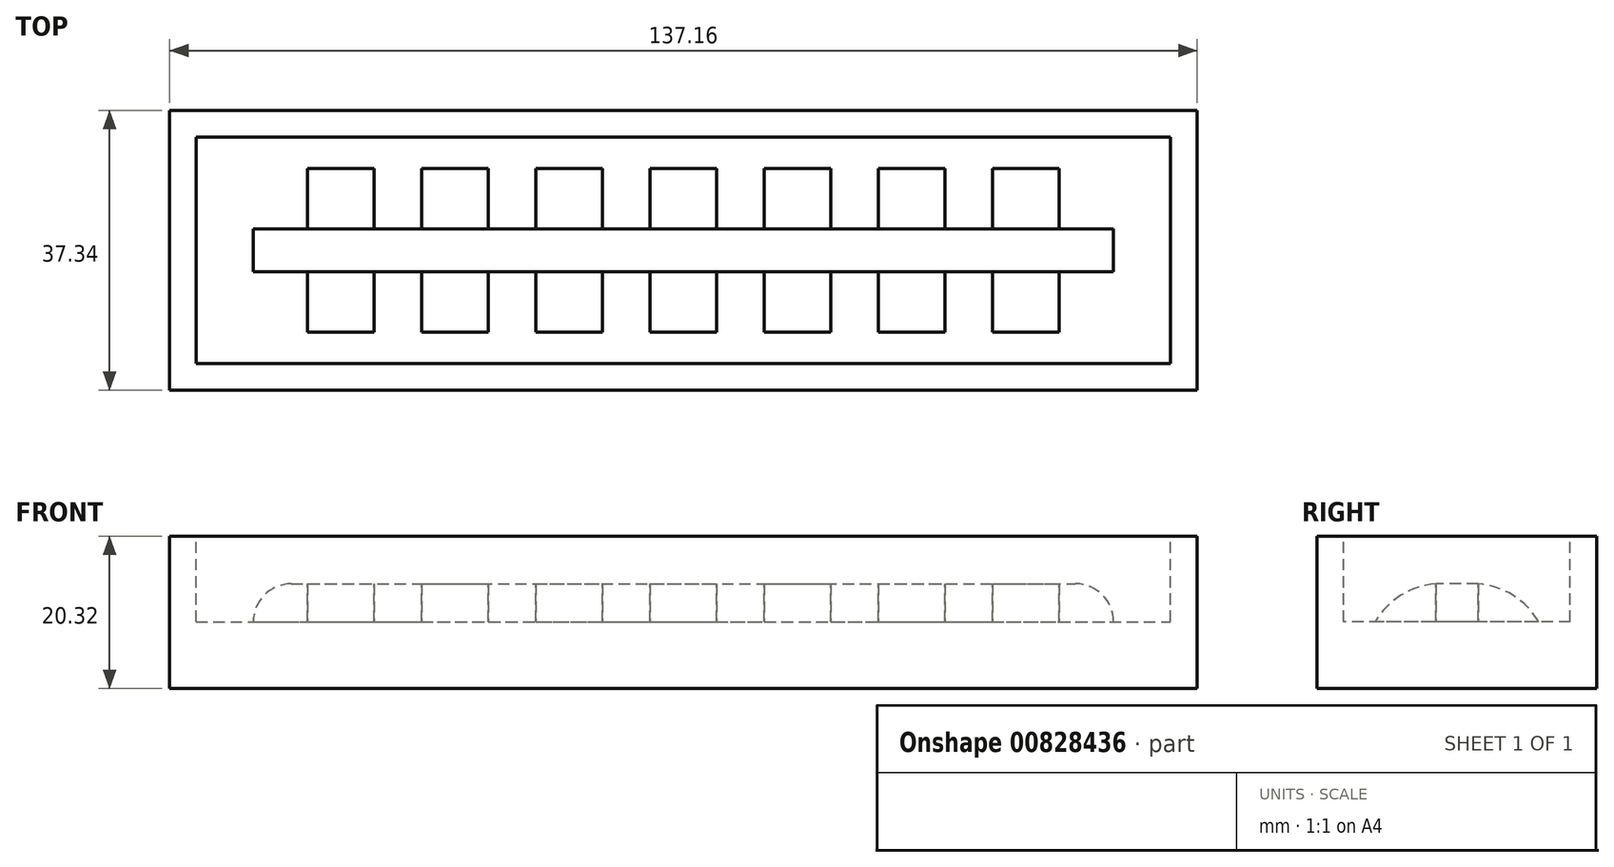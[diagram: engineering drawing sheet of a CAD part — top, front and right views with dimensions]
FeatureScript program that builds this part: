
annotation { "Feature Type Name" : "Feature", "Feature Type Description" : "" }
export const myFeature = defineFeature(function(context is Context, id is Id, definition is map)
    precondition{}
    {
        {
            var Q0;
            Q0=qCreatedBy(makeId("Top.planeOp"),FACE);
            var sketch = newSketch(context, id + "F0", { "sketchPlane" : qUnion([Q0])});
            skLineSegment(sketch, "E0.bottom", {"start": v(-68.58, 18.67) * mm, "end": v(68.58, 18.67) * mm});
            skLineSegment(sketch, "E0.top", {"start": v(-68.58, -18.67) * mm, "end": v(68.58, -18.67) * mm});
            skLineSegment(sketch, "E0.left", {"start": v(-68.58, 18.67) * mm, "end": v(-68.58, -18.67) * mm});
            skLineSegment(sketch, "E0.right", {"start": v(68.58, 18.67) * mm, "end": v(68.58, -18.67) * mm});
            skPoint(sketch, "E0.middle", {"position": v(0, 0) * mm});
            skSolve(sketch);
        }
        {
            var Q0;
            Q0=makeQuery(id+"F0.imprint","IMPRINT",FACE,{"disambiguationData":[TD([[makeQuery(id+"F0.imprint","IMPRINT",EDGE,{"derivedFrom":sQuery(id+"F0.wireOp",EDGE,"E0.bottom")}),-1.0]])]});
            extrude(context, id + "F1", {"entities" : qUnion([Q0]), "depth" : 20.32 * mm, "offsetDistance" : 25.4 * mm});
        }
        {
            var Q0;
            Q0=makeQuery(id+"F1.opExtrude","CAP_FACE",FACE,{"disambiguationData":[OSD([sQuery(id+"F0.wireOp",EDGE,"E0.bottom"),sQuery(id+"F0.wireOp",EDGE,"E0.top"),sQuery(id+"F0.wireOp",EDGE,"E0.left"),sQuery(id+"F0.wireOp",EDGE,"E0.right")])],"isStart":false});
            var sketch = newSketch(context, id + "F2", { "sketchPlane" : qUnion([Q0])});
            skLineSegment(sketch, "E1.bottom", {"start": v(-65.02, 15.11) * mm, "end": v(65.02, 15.11) * mm});
            skLineSegment(sketch, "E1.top", {"start": v(-65.02, -15.11) * mm, "end": v(65.02, -15.11) * mm});
            skLineSegment(sketch, "E1.left", {"start": v(-65.02, 15.11) * mm, "end": v(-65.02, -15.11) * mm});
            skLineSegment(sketch, "E1.right", {"start": v(65.02, 15.11) * mm, "end": v(65.02, -15.11) * mm});
            skPoint(sketch, "E1.middle", {"position": v(0, 0) * mm});
            skSolve(sketch);
        }
        {
            var Q0;
            Q0 = qSketchRegion(id + "F2", true);
            extrude(context, id + "F3", {"entities" : qUnion([Q0]), "operationType" : NewBodyOperationType.REMOVE, "oppositeDirection" : true, "depth" : 11.43 * mm, "offsetDistance" : 25.4 * mm});
        }
        {
            var Q0;
            Q0=makeQuery(id+"F3.boolean.opBoolean","COPY",FACE,{"derivedFrom":makeQuery(id+"F3.opExtrude","CAP_FACE",FACE,{"disambiguationData":[OSD([sQuery(id+"F2.wireOp",EDGE,"E1.bottom"),sQuery(id+"F2.wireOp",EDGE,"E1.top"),sQuery(id+"F2.wireOp",EDGE,"E1.left"),sQuery(id+"F2.wireOp",EDGE,"E1.right")])],"isStart":false})});
            var sketch = newSketch(context, id + "F4", { "sketchPlane" : qUnion([Q0])});
            skLineSegment(sketch, "E2.bottom", {"start": v(-4.44, 10.92) * mm, "end": v(4.45, 10.92) * mm});
            skLineSegment(sketch, "E2.top", {"start": v(-4.44, -10.92) * mm, "end": v(4.45, -10.92) * mm});
            skLineSegment(sketch, "E2.left", {"start": v(-4.44, 10.92) * mm, "end": v(-4.44, -10.92) * mm});
            skLineSegment(sketch, "E2.right", {"start": v(4.45, 10.92) * mm, "end": v(4.45, -10.92) * mm});
            skPoint(sketch, "E2.middle", {"position": v(0, 0) * mm});
            skPoint(sketch, "E3.endSnap0", {"position": v(0, -10.92) * mm});
            skPoint(sketch, "E4", {"position": v(-54.86, 0) * mm});
            skPoint(sketch, "E5", {"position": v(-45.72, 0) * mm});
            skPoint(sketch, "E6", {"position": v(-30.48, 0) * mm});
            skPoint(sketch, "E7", {"position": v(-15.24, 0) * mm});
            skPoint(sketch, "E8", {"position": v(15.24, 0) * mm});
            skPoint(sketch, "E8.positionSnap0", {"position": v(-4.44, 0) * mm});
            skPoint(sketch, "E9", {"position": v(30.48, 0) * mm});
            skPoint(sketch, "E10", {"position": v(45.72, 0) * mm});
            skPoint(sketch, "E11", {"position": v(54.86, 0) * mm});
            skLineSegment(sketch, "E12.bottom", {"start": v(10.8, 10.92) * mm, "end": v(19.69, 10.92) * mm});
            skLineSegment(sketch, "E12.top", {"start": v(10.8, -10.92) * mm, "end": v(19.69, -10.92) * mm});
            skLineSegment(sketch, "E12.left", {"start": v(10.8, 10.92) * mm, "end": v(10.8, -10.92) * mm});
            skLineSegment(sketch, "E12.right", {"start": v(19.69, 10.92) * mm, "end": v(19.69, -10.92) * mm});
            skLineSegment(sketch, "E13.bottom", {"start": v(26.03, 10.92) * mm, "end": v(34.92, 10.92) * mm});
            skLineSegment(sketch, "E13.top", {"start": v(26.03, -10.92) * mm, "end": v(34.92, -10.92) * mm});
            skLineSegment(sketch, "E13.left", {"start": v(26.03, 10.92) * mm, "end": v(26.03, -10.92) * mm});
            skLineSegment(sketch, "E13.right", {"start": v(34.92, 10.92) * mm, "end": v(34.92, -10.92) * mm});
            skLineSegment(sketch, "E14.bottom", {"start": v(41.27, 10.92) * mm, "end": v(50.16, 10.92) * mm});
            skLineSegment(sketch, "E14.top", {"start": v(41.27, -10.92) * mm, "end": v(50.16, -10.92) * mm});
            skLineSegment(sketch, "E14.left", {"start": v(41.27, 10.92) * mm, "end": v(41.27, -10.92) * mm});
            skLineSegment(sketch, "E14.right", {"start": v(50.16, 10.92) * mm, "end": v(50.16, -10.92) * mm});
            skLineSegment(sketch, "E15.bottom", {"start": v(-19.69, 10.92) * mm, "end": v(-10.8, 10.92) * mm});
            skLineSegment(sketch, "E15.top", {"start": v(-19.69, -10.92) * mm, "end": v(-10.8, -10.92) * mm});
            skLineSegment(sketch, "E15.left", {"start": v(-19.69, 10.92) * mm, "end": v(-19.69, -10.92) * mm});
            skLineSegment(sketch, "E15.right", {"start": v(-10.8, 10.92) * mm, "end": v(-10.8, -10.92) * mm});
            skLineSegment(sketch, "E16.bottom", {"start": v(-34.92, 10.92) * mm, "end": v(-26.04, 10.92) * mm});
            skLineSegment(sketch, "E16.top", {"start": v(-34.92, -10.92) * mm, "end": v(-26.04, -10.92) * mm});
            skLineSegment(sketch, "E16.left", {"start": v(-34.92, 10.92) * mm, "end": v(-34.92, -10.92) * mm});
            skLineSegment(sketch, "E16.right", {"start": v(-26.04, 10.92) * mm, "end": v(-26.04, -10.92) * mm});
            skLineSegment(sketch, "E17.bottom", {"start": v(-50.16, 10.92) * mm, "end": v(-41.28, 10.92) * mm});
            skLineSegment(sketch, "E17.top", {"start": v(-50.16, -10.92) * mm, "end": v(-41.28, -10.92) * mm});
            skLineSegment(sketch, "E17.left", {"start": v(-50.16, 10.92) * mm, "end": v(-50.16, -10.92) * mm});
            skLineSegment(sketch, "E17.right", {"start": v(-41.27, 10.92) * mm, "end": v(-41.27, -10.92) * mm});
            skSolve(sketch);
        }
        {
            var Q0;
            Q0 = qSketchRegion(id + "F4", true);
            extrude(context, id + "F5", {"entities" : qUnion([Q0]), "operationType" : NewBodyOperationType.ADD, "depth" : 5.08 * mm, "offsetDistance" : 25.4 * mm});
        }
        {
            var Q0;
            Q0=makeQuery(id+"F5.opExtrude","CAP_EDGE",EDGE,{"disambiguationData":[OSD([sQuery(id+"F4.wireOp",EDGE,"E17.top")])],"isStart":false});
            var Q1;
            Q1=makeQuery(id+"F5.opExtrude","CAP_EDGE",EDGE,{"disambiguationData":[OSD([sQuery(id+"F4.wireOp",EDGE,"E16.top")])],"isStart":false});
            var Q2;
            Q2=makeQuery(id+"F5.opExtrude","CAP_EDGE",EDGE,{"disambiguationData":[OSD([sQuery(id+"F4.wireOp",EDGE,"E15.top")])],"isStart":false});
            var Q3;
            Q3=makeQuery(id+"F5.opExtrude","CAP_EDGE",EDGE,{"disambiguationData":[OSD([sQuery(id+"F4.wireOp",EDGE,"E2.top")])],"isStart":false});
            var Q4;
            Q4=makeQuery(id+"F5.opExtrude","CAP_EDGE",EDGE,{"disambiguationData":[OSD([sQuery(id+"F4.wireOp",EDGE,"E12.top")])],"isStart":false});
            var Q5;
            Q5=makeQuery(id+"F5.opExtrude","CAP_EDGE",EDGE,{"disambiguationData":[OSD([sQuery(id+"F4.wireOp",EDGE,"E13.top")])],"isStart":false});
            var Q6;
            Q6=makeQuery(id+"F5.opExtrude","CAP_EDGE",EDGE,{"disambiguationData":[OSD([sQuery(id+"F4.wireOp",EDGE,"E14.top")])],"isStart":false});
            var Q7;
            Q7=makeQuery(id+"F5.opExtrude","CAP_EDGE",EDGE,{"disambiguationData":[OSD([sQuery(id+"F4.wireOp",EDGE,"mSEgQNew-V41t-byaO-6fER-Ci8ijIq9LOAr.top")])],"isStart":false});
            var Q8;
            Q8=makeQuery(id+"F5.opExtrude","CAP_EDGE",EDGE,{"disambiguationData":[OSD([sQuery(id+"F4.wireOp",EDGE,"mSEgQNew-V41t-byaO-6fER-Ci8ijIq9LOAr.bottom")])],"isStart":false});
            var Q9;
            Q9=makeQuery(id+"F5.opExtrude","CAP_EDGE",EDGE,{"disambiguationData":[OSD([sQuery(id+"F4.wireOp",EDGE,"E14.bottom")])],"isStart":false});
            var Q10;
            Q10=makeQuery(id+"F5.opExtrude","CAP_EDGE",EDGE,{"disambiguationData":[OSD([sQuery(id+"F4.wireOp",EDGE,"E13.bottom")])],"isStart":false});
            var Q11;
            Q11=makeQuery(id+"F5.opExtrude","CAP_EDGE",EDGE,{"disambiguationData":[OSD([sQuery(id+"F4.wireOp",EDGE,"E12.bottom")])],"isStart":false});
            var Q12;
            Q12=makeQuery(id+"F5.opExtrude","CAP_EDGE",EDGE,{"disambiguationData":[OSD([sQuery(id+"F4.wireOp",EDGE,"E2.bottom")])],"isStart":false});
            var Q13;
            Q13=makeQuery(id+"F5.opExtrude","CAP_EDGE",EDGE,{"disambiguationData":[OSD([sQuery(id+"F4.wireOp",EDGE,"E15.bottom")])],"isStart":false});
            var Q14;
            Q14=makeQuery(id+"F5.opExtrude","CAP_EDGE",EDGE,{"disambiguationData":[OSD([sQuery(id+"F4.wireOp",EDGE,"E16.bottom")])],"isStart":false});
            var Q15;
            Q15=makeQuery(id+"F5.opExtrude","CAP_EDGE",EDGE,{"disambiguationData":[OSD([sQuery(id+"F4.wireOp",EDGE,"E17.bottom")])],"isStart":false});
            var Q16;
            Q16=makeQuery(id+"F5.opExtrude","CAP_EDGE",EDGE,{"disambiguationData":[OSD([sQuery(id+"F4.wireOp",EDGE,"LUGdPy4v-zDzo-tgnP-LAKF-R8VeouCf35KK.bottom")])],"isStart":false});
            var Q17;
            Q17=makeQuery(id+"F5.opExtrude","CAP_EDGE",EDGE,{"disambiguationData":[OSD([sQuery(id+"F4.wireOp",EDGE,"LUGdPy4v-zDzo-tgnP-LAKF-R8VeouCf35KK.top")])],"isStart":false});
            fillet(context, id + "F6", {"entities" : qUnion([Q0, Q1, Q2, Q3, Q4, Q5, Q6, Q7, Q8, Q9, Q10, Q11, Q12, Q13, Q14, Q15, Q16, Q17]), "radius" : 10.16 * mm, "tangentPropagation" : true, "allowEdgeOverflow" : false});
        }
        {
            var Q0;
            Q0=makeQuery(id+"F3.boolean.opBoolean","COPY",FACE,{"derivedFrom":makeQuery(id+"F3.opExtrude","CAP_FACE",FACE,{"disambiguationData":[OSD([sQuery(id+"F2.wireOp",EDGE,"E1.bottom"),sQuery(id+"F2.wireOp",EDGE,"E1.top"),sQuery(id+"F2.wireOp",EDGE,"E1.left"),sQuery(id+"F2.wireOp",EDGE,"E1.right")])],"isStart":false})});
            var sketch = newSketch(context, id + "F7", { "sketchPlane" : qUnion([Q0])});
            skLineSegment(sketch, "E18.bottom", {"start": v(-57.42, 2.83) * mm, "end": v(57.42, 2.83) * mm});
            skLineSegment(sketch, "E18.top", {"start": v(-57.42, -2.83) * mm, "end": v(57.42, -2.83) * mm});
            skLineSegment(sketch, "E18.left", {"start": v(-57.42, 2.83) * mm, "end": v(-57.42, -2.83) * mm});
            skLineSegment(sketch, "E18.right", {"start": v(57.42, 2.83) * mm, "end": v(57.42, -2.83) * mm});
            skPoint(sketch, "E18.middle", {"position": v(0, 0) * mm});
            skSolve(sketch);
        }
        {
            var Q0;
            {var subQ0=sQuery(id+"F7.wireOp",EDGE,"E18.left");Q0=makeQuery(id+"F7.imprint","IMPRINT",FACE,{"disambiguationData":[TD([[makeQuery(id+"F7.imprint","IMPRINT",EDGE,{"derivedFrom":subQ0}),1.0]])]});}
            var Q1;
            {var subQ0=sQuery(id+"F7.wireOp",EDGE,"E18.bottom");var subQ1=makeQuery(id+"F5.opExtrude","CAP_EDGE",EDGE,{"disambiguationData":[OSD([sQuery(id+"F4.wireOp",EDGE,"E17.right")])],"isStart":true});var subQ2=makeQuery(id+"F7.imprint","INTERSECT",VERTEX,{"derivedFrom":[subQ1,subQ0]});Q1=makeQuery(id+"F7.imprint","IMPRINT",FACE,{"disambiguationData":[TD([[makeQuery(id+"F7.imprint","IMPRINT",EDGE,{"disambiguationData":[TD([[subQ2,-1.0]])],"derivedFrom":subQ0}),-1.0]])]});}
            var Q2;
            {var subQ0=sQuery(id+"F7.wireOp",EDGE,"E18.bottom");var subQ1=makeQuery(id+"F5.opExtrude","CAP_EDGE",EDGE,{"disambiguationData":[OSD([sQuery(id+"F4.wireOp",EDGE,"E16.right")])],"isStart":true});var subQ2=makeQuery(id+"F7.imprint","INTERSECT",VERTEX,{"derivedFrom":[subQ1,subQ0]});Q2=makeQuery(id+"F7.imprint","IMPRINT",FACE,{"disambiguationData":[TD([[makeQuery(id+"F7.imprint","IMPRINT",EDGE,{"disambiguationData":[TD([[subQ2,-1.0]])],"derivedFrom":subQ0}),-1.0]])]});}
            var Q3;
            {var subQ0=sQuery(id+"F7.wireOp",EDGE,"E18.bottom");var subQ1=makeQuery(id+"F5.opExtrude","CAP_EDGE",EDGE,{"disambiguationData":[OSD([sQuery(id+"F4.wireOp",EDGE,"E15.right")])],"isStart":true});var subQ2=makeQuery(id+"F7.imprint","INTERSECT",VERTEX,{"derivedFrom":[subQ1,subQ0]});Q3=makeQuery(id+"F7.imprint","IMPRINT",FACE,{"disambiguationData":[TD([[makeQuery(id+"F7.imprint","IMPRINT",EDGE,{"disambiguationData":[TD([[subQ2,-1.0]])],"derivedFrom":subQ0}),-1.0]])]});}
            var Q4;
            {var subQ0=sQuery(id+"F7.wireOp",EDGE,"E18.bottom");var subQ1=makeQuery(id+"F5.opExtrude","CAP_EDGE",EDGE,{"disambiguationData":[OSD([sQuery(id+"F4.wireOp",EDGE,"E2.right")])],"isStart":true});var subQ2=makeQuery(id+"F7.imprint","INTERSECT",VERTEX,{"derivedFrom":[subQ1,subQ0]});Q4=makeQuery(id+"F7.imprint","IMPRINT",FACE,{"disambiguationData":[TD([[makeQuery(id+"F7.imprint","IMPRINT",EDGE,{"disambiguationData":[TD([[subQ2,-1.0]])],"derivedFrom":subQ0}),-1.0]])]});}
            var Q5;
            {var subQ0=sQuery(id+"F7.wireOp",EDGE,"E18.bottom");var subQ1=makeQuery(id+"F5.opExtrude","CAP_EDGE",EDGE,{"disambiguationData":[OSD([sQuery(id+"F4.wireOp",EDGE,"E12.right")])],"isStart":true});var subQ2=makeQuery(id+"F7.imprint","INTERSECT",VERTEX,{"derivedFrom":[subQ1,subQ0]});Q5=makeQuery(id+"F7.imprint","IMPRINT",FACE,{"disambiguationData":[TD([[makeQuery(id+"F7.imprint","IMPRINT",EDGE,{"disambiguationData":[TD([[subQ2,-1.0]])],"derivedFrom":subQ0}),-1.0]])]});}
            var Q6;
            {var subQ0=sQuery(id+"F7.wireOp",EDGE,"E18.bottom");var subQ1=makeQuery(id+"F5.opExtrude","CAP_EDGE",EDGE,{"disambiguationData":[OSD([sQuery(id+"F4.wireOp",EDGE,"E13.right")])],"isStart":true});var subQ2=makeQuery(id+"F7.imprint","INTERSECT",VERTEX,{"derivedFrom":[subQ1,subQ0]});Q6=makeQuery(id+"F7.imprint","IMPRINT",FACE,{"disambiguationData":[TD([[makeQuery(id+"F7.imprint","IMPRINT",EDGE,{"disambiguationData":[TD([[subQ2,-1.0]])],"derivedFrom":subQ0}),-1.0]])]});}
            var Q7;
            {var subQ0=sQuery(id+"F7.wireOp",EDGE,"E18.right");Q7=makeQuery(id+"F7.imprint","IMPRINT",FACE,{"disambiguationData":[TD([[makeQuery(id+"F7.imprint","IMPRINT",EDGE,{"derivedFrom":subQ0}),-1.0]])]});}
            extrude(context, id + "F8", {"entities" : qUnion([Q0, Q1, Q2, Q3, Q4, Q5, Q6, Q7]), "operationType" : NewBodyOperationType.ADD, "depth" : 5.08 * mm, "offsetDistance" : 25.4 * mm});
        }
        {
            var Q0;
            Q0=makeQuery(id+"F8.opExtrude","CAP_EDGE",EDGE,{"disambiguationData":[OSD([sQuery(id+"F7.wireOp",EDGE,"E18.left")])],"isStart":false});
            var Q1;
            Q1=makeQuery(id+"F8.opExtrude","CAP_EDGE",EDGE,{"disambiguationData":[OSD([sQuery(id+"F7.wireOp",EDGE,"E18.right")])],"isStart":false});
            fillet(context, id + "F9", {"entities" : qUnion([Q0, Q1]), "radius" : 5.08 * mm, "tangentPropagation" : true, "allowEdgeOverflow" : false});
        }
    });
